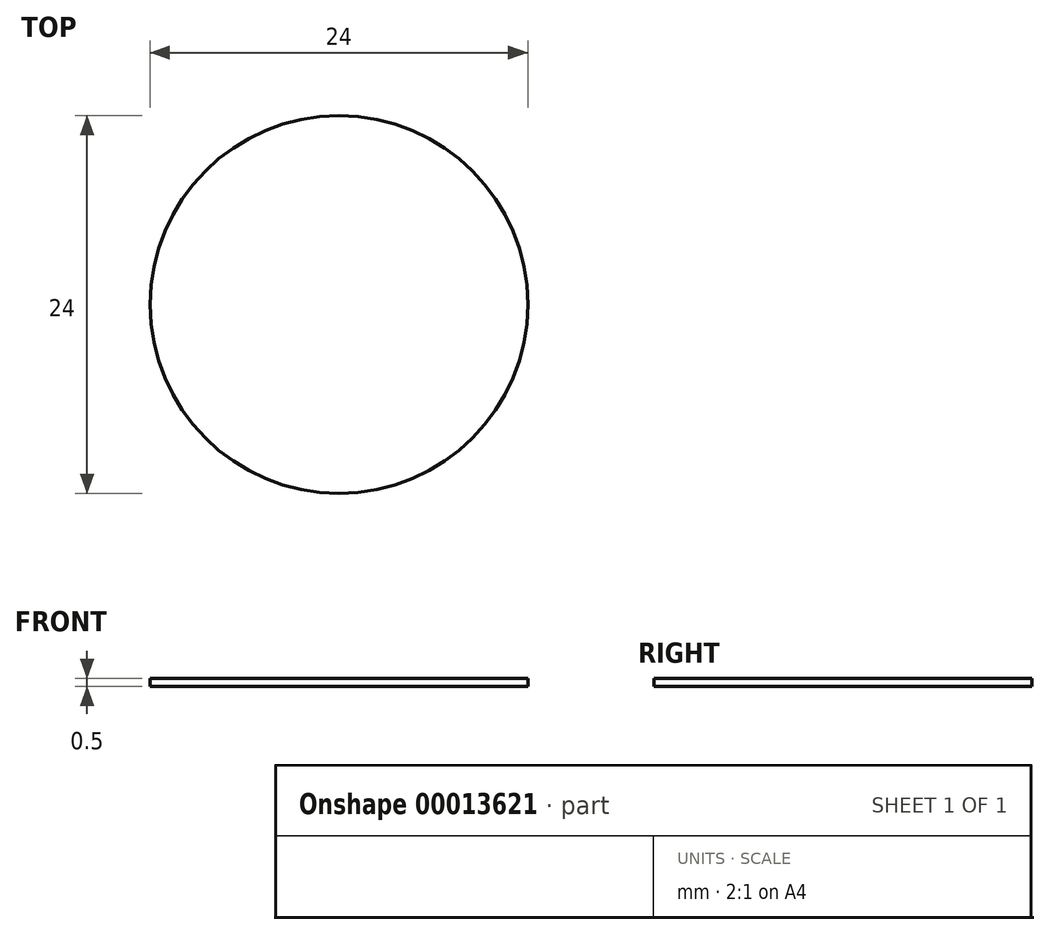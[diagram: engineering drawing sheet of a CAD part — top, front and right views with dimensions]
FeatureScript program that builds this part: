
annotation { "Feature Type Name" : "Feature", "Feature Type Description" : "" }
export const myFeature = defineFeature(function(context is Context, id is Id, definition is map)
    precondition{}
    {
        {
            var Q0;
            Q0=qCreatedBy(makeId("Top.planeOp"),FACE);
            var sketch = newSketch(context, id + "F0", { "sketchPlane" : qUnion([Q0])});
            skCircle(sketch, "E0", {"center": v(0, 0) * mm, "radius": 12 * mm});
            skSolve(sketch);
        }
        {
            var Q0;
            Q0=makeQuery(id+"F0.imprint","IMPRINT",FACE,{"disambiguationData":[TD([[makeQuery(id+"F0.imprint","IMPRINT",EDGE,{"derivedFrom":sQuery(id+"F0.wireOp",EDGE,"E0")}),1.0]])]});
            extrude(context, id + "F1", {"entities" : qUnion([Q0]), "depth" : .5 * mm});
        }
    });
